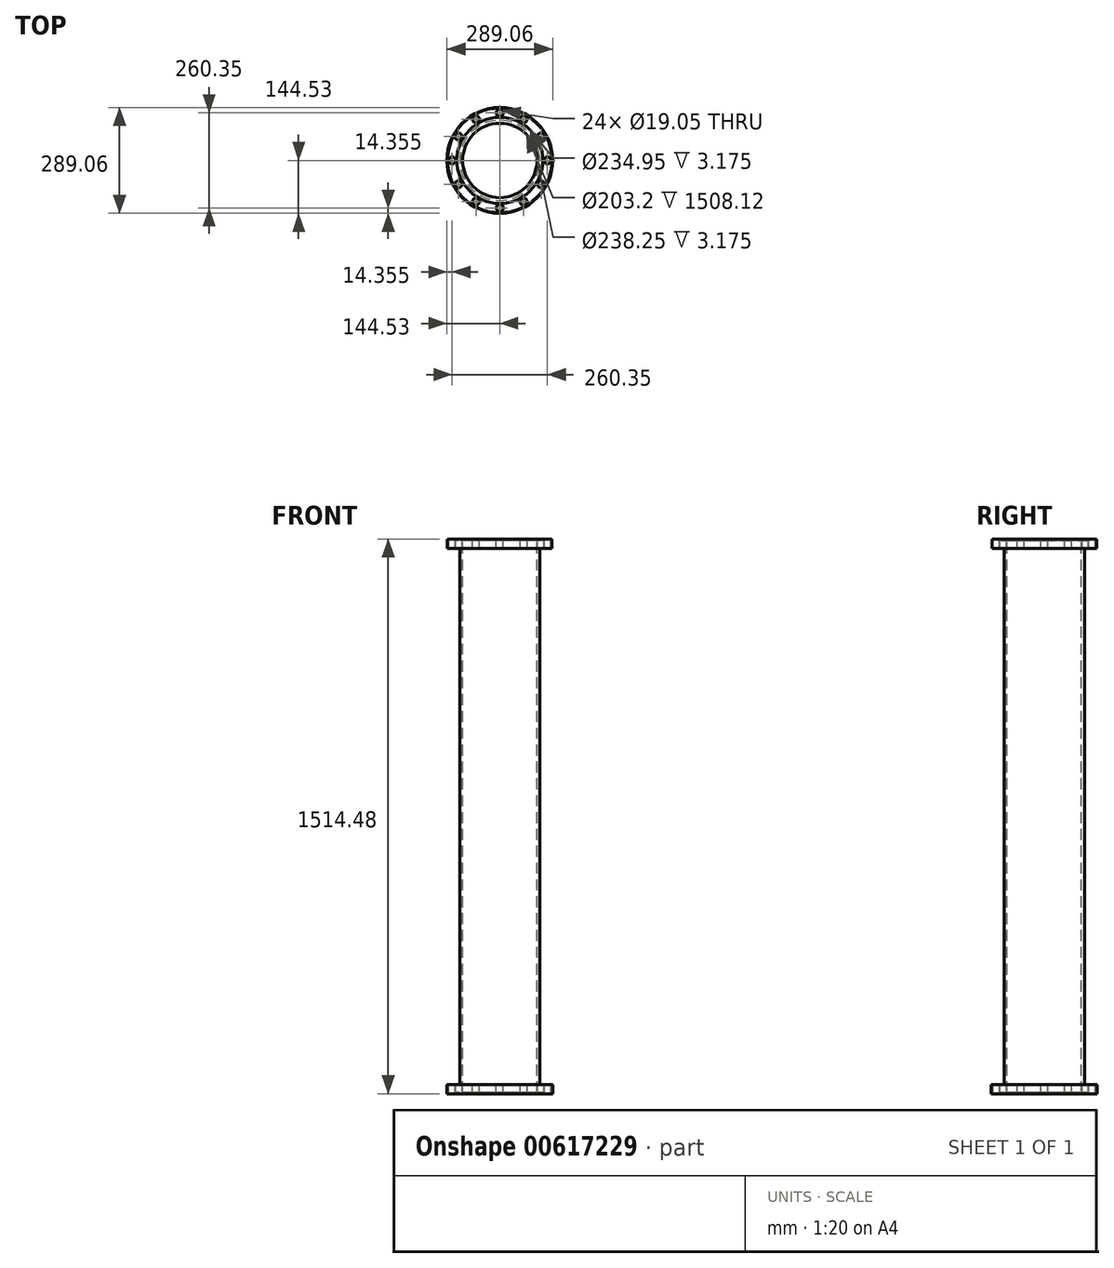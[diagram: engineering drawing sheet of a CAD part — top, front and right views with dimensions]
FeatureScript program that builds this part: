
annotation { "Feature Type Name" : "Feature", "Feature Type Description" : "" }
export const myFeature = defineFeature(function(context is Context, id is Id, definition is map)
    precondition{}
    {
        {
            var Q0;
            Q0=qCreatedBy(makeId("Front.planeOp"),FACE);
            var sketch = newSketch(context, id + "F0", { "sketchPlane" : qUnion([Q0])});
            skLineSegment(sketch, "E0", {"start": v(109.6, 0) * mm, "end": v(142.88, 0) * mm});
            skLineSegment(sketch, "E1", {"start": v(142.88, 0) * mm, "end": v(142.88, 25.4) * mm});
            skLineSegment(sketch, "E2", {"start": v(117.48, 25.4) * mm, "end": v(117.48, 22.23) * mm});
            skLineSegment(sketch, "E3", {"start": v(117.48, 22.22) * mm, "end": v(101.6, 22.22) * mm});
            skLineSegment(sketch, "E4", {"start": v(101.6, 22.22) * mm, "end": v(101.6, 15.88) * mm});
            skLineSegment(sketch, "E5", {"start": v(117.48, 25.4) * mm, "end": v(142.88, 25.4) * mm});
            skLineSegment(sketch, "E6.trimOffspring", {"start": v(101.6, 22.23) * mm, "end": v(101.6, 15.88) * mm});
            skLineSegment(sketch, "E7", {"start": v(101.6, 15.88) * mm, "end": v(109.6, 15.88) * mm});
            skLineSegment(sketch, "E8", {"start": v(109.6, 15.88) * mm, "end": v(109.6, 0) * mm});
            skPoint(sketch, "E9.endSnap0", {"position": v(101.6, 19.05) * mm});
            skLineSegment(sketch, "E10.MirrorCS", {"start": v(119.13, -1489.08) * mm, "end": v(119.13, -1485.9) * mm});
            skLineSegment(sketch, "E11.MirrorCS", {"start": v(101.6, -1485.9) * mm, "end": v(101.6, -1479.55) * mm});
            skPoint(sketch, "E12.MirrorP", {"position": v(101.6, -1482.73) * mm});
            skLineSegment(sketch, "E13.MirrorCS", {"start": v(101.6, -1479.55) * mm, "end": v(109.6, -1479.55) * mm});
            skPoint(sketch, "E14.MirrorP", {"position": v(101.6, -1489.08) * mm});
            skLineSegment(sketch, "E15.MirrorCS", {"start": v(119.13, -1489.08) * mm, "end": v(144.53, -1489.08) * mm});
            skLineSegment(sketch, "E16.MirrorCS", {"start": v(119.13, -1485.9) * mm, "end": v(101.6, -1485.9) * mm});
            skLineSegment(sketch, "E17.MirrorCS", {"start": v(109.6, -1463.68) * mm, "end": v(144.53, -1463.68) * mm});
            skLineSegment(sketch, "E18.MirrorCS", {"start": v(109.6, -1479.55) * mm, "end": v(109.6, -1463.68) * mm});
            skLineSegment(sketch, "E19.MirrorCS", {"start": v(144.53, -1463.68) * mm, "end": v(144.53, -1489.08) * mm});
            skLineSegment(sketch, "E20.left", {"start": v(101.6, 15.87) * mm, "end": v(101.6, -1479.55) * mm});
            skLineSegment(sketch, "E20.right", {"start": v(109.6, 15.87) * mm, "end": v(109.6, -1479.55) * mm});
            skLineSegment(sketch, "E21", {"start": v(0, 68.5) * mm, "end": v(0, -49) * mm, "construction": true});
            skSolve(sketch);
        }
        {
            var Q0;
            Q0 = qSketchRegion(id + "F0", true);
            var Q1;
            Q1=sQuery(id+"F0.wireOp",EDGE,"E21");
            revolve(context, id + "F1", {"entities" : qUnion([Q0]), "axis" : qUnion([Q1]), "revolveType" : RevolveType.FULL});
        }
        {
            var Q0;
            Q0=makeQuery(id+"F1.opRevolve","SWEPT_FACE",FACE,{"disambiguationData":[OSD([sQuery(id+"F0.wireOp",EDGE,"E5")])]});
            var sketch = newSketch(context, id + "F2", { "sketchPlane" : qUnion([Q0])});
            skCircle(sketch, "E22", {"center": v(130.18, 0) * mm, "radius": 9.53 * mm});
            skCircle(sketch, "E23.1.0", {"center": v(112.73, 65.09) * mm, "radius": 9.53 * mm});
            skCircle(sketch, "E23.2.0", {"center": v(65.09, 112.73) * mm, "radius": 9.53 * mm});
            skCircle(sketch, "E23.3.0", {"center": v(0, 130.18) * mm, "radius": 9.53 * mm});
            skCircle(sketch, "E23.4.0", {"center": v(-65.09, 112.73) * mm, "radius": 9.53 * mm});
            skCircle(sketch, "E23.5.0", {"center": v(-112.73, 65.09) * mm, "radius": 9.53 * mm});
            skCircle(sketch, "E23.6.0", {"center": v(-130.18, 0) * mm, "radius": 9.53 * mm});
            skCircle(sketch, "E23.7.0", {"center": v(-112.73, -65.09) * mm, "radius": 9.53 * mm});
            skCircle(sketch, "E23.8.0", {"center": v(-65.09, -112.73) * mm, "radius": 9.53 * mm});
            skCircle(sketch, "E23.9.0", {"center": v(0, -130.18) * mm, "radius": 9.53 * mm});
            skCircle(sketch, "E23.10.0", {"center": v(65.09, -112.73) * mm, "radius": 9.53 * mm});
            skCircle(sketch, "E23.11.0", {"center": v(112.73, -65.09) * mm, "radius": 9.53 * mm});
            skPoint(sketch, "E23.center", {"position": v(0, 0) * mm});
            skSolve(sketch);
        }
        {
            var Q0;
            Q0 = qSketchRegion(id + "F2", true);
            extrude(context, id + "F3", {"entities" : qUnion([Q0]), "operationType" : NewBodyOperationType.REMOVE, "endBound" : BoundingType.THROUGH_ALL, "oppositeDirection" : true, "depth" : 25.4 * mm, "offsetDistance" : 25.4 * mm});
        }
    });
